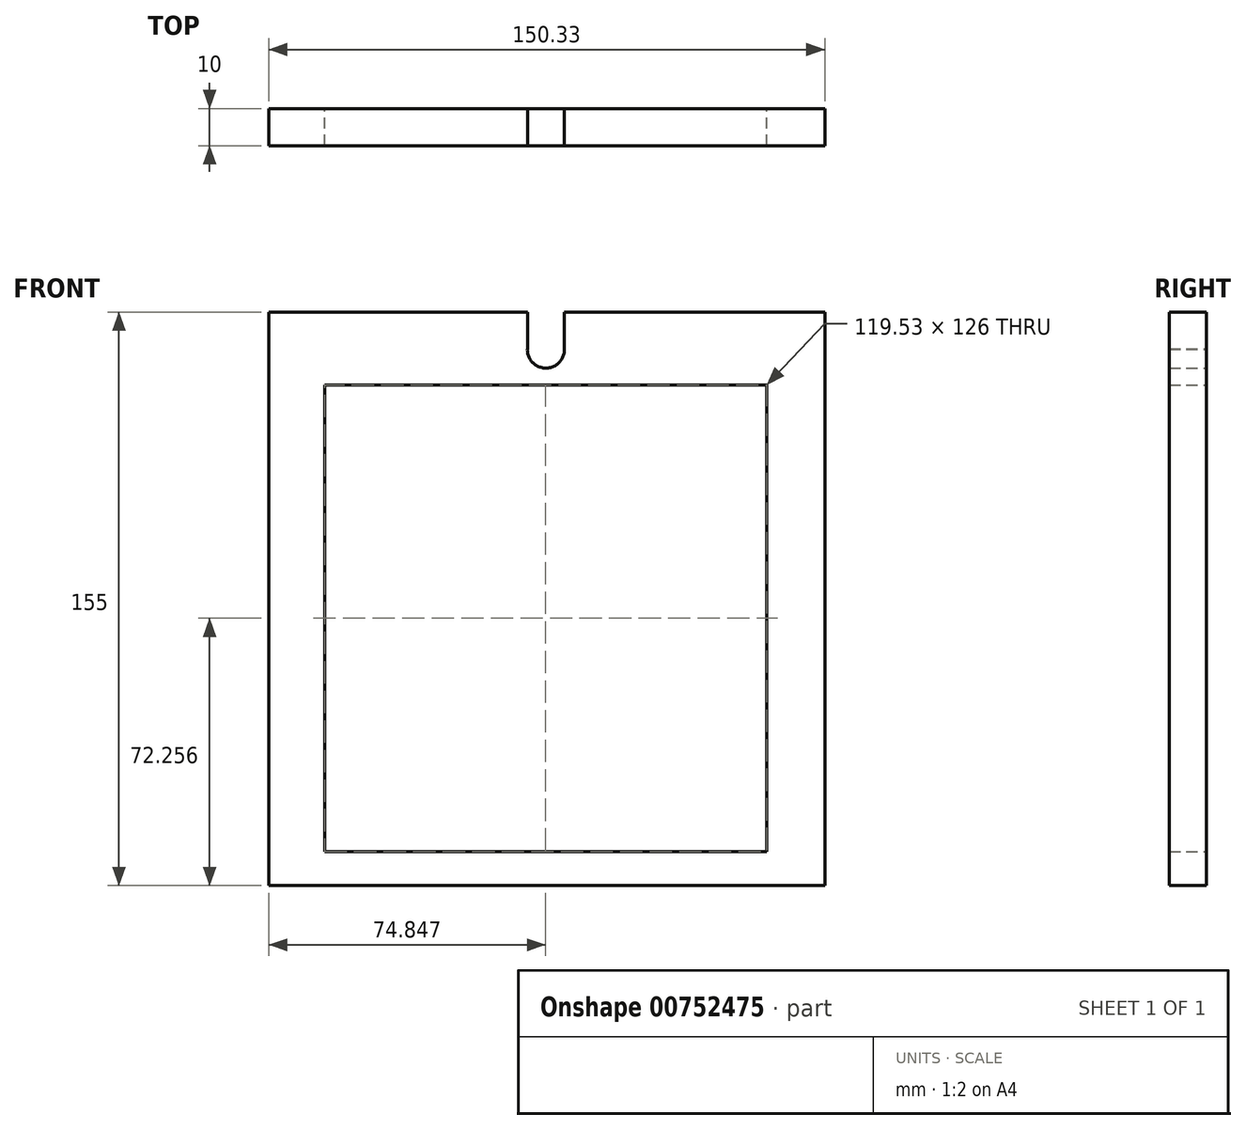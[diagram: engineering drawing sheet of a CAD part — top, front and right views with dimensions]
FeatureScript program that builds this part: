
annotation { "Feature Type Name" : "Feature", "Feature Type Description" : "" }
export const myFeature = defineFeature(function(context is Context, id is Id, definition is map)
    precondition{}
    {
        {
            var Q0;
            Q0=qCreatedBy(makeId("Front.planeOp"),FACE);
            var sketch = newSketch(context, id + "F0", { "sketchPlane" : qUnion([Q0])});
            skLineSegment(sketch, "E0.bottom", {"start": v(-59.85, 57.86) * mm, "end": v(59.68, 57.86) * mm});
            skLineSegment(sketch, "E0.top", {"start": v(-59.85, -68.14) * mm, "end": v(59.68, -68.14) * mm});
            skLineSegment(sketch, "E0.left", {"start": v(-59.85, 57.86) * mm, "end": v(-59.85, -68.14) * mm});
            skLineSegment(sketch, "E0.right", {"start": v(59.68, 57.86) * mm, "end": v(59.68, -68.14) * mm});
            skLineSegment(sketch, "E1.bottom", {"start": v(-74.93, 77.6) * mm, "end": v(75.4, 77.6) * mm});
            skLineSegment(sketch, "E1.top", {"start": v(-74.93, -77.4) * mm, "end": v(75.4, -77.4) * mm});
            skLineSegment(sketch, "E1.left", {"start": v(-74.93, 77.6) * mm, "end": v(-74.93, -77.4) * mm});
            skLineSegment(sketch, "E1.right", {"start": v(75.4, 77.6) * mm, "end": v(75.4, -77.4) * mm});
            skArc(sketch, "E2", {"start": v(-5, 67.7) * mm, "mid": v(-0.05, 62.48) * mm, "end": v(5, 67.59) * mm});
            skLineSegment(sketch, "E3", {"start": v(-5, 67.7) * mm, "end": v(-5, 77.6) * mm});
            skLineSegment(sketch, "E4", {"start": v(5, 67.59) * mm, "end": v(5, 77.6) * mm});
            skSolve(sketch);
        }
        {
            var Q0;
            Q0=makeQuery(id+"F0.imprint","IMPRINT",FACE,{"disambiguationData":[TD([[makeQuery(id+"F0.imprint","IMPRINT",EDGE,{"derivedFrom":sQuery(id+"F0.wireOp",EDGE,"E0.bottom")}),1.0]])]});
            extrude(context, id + "F1", {"entities" : qUnion([Q0]), "endBound" : BoundingType.SYMMETRIC, "depth" : 10 * mm, "offsetDistance" : 25 * mm});
        }
    });
